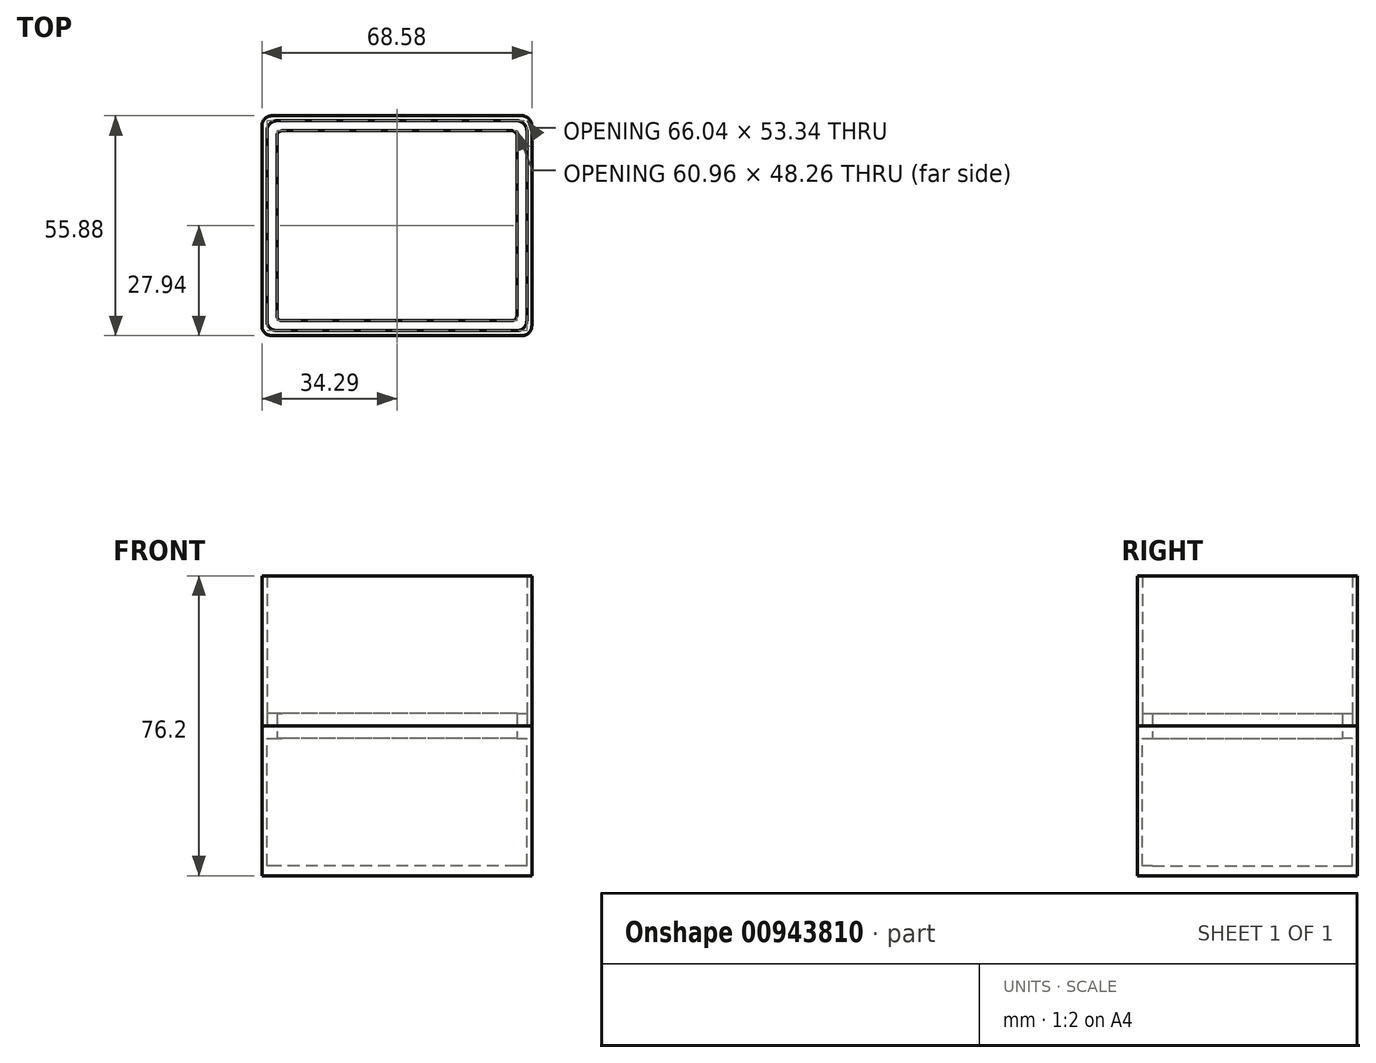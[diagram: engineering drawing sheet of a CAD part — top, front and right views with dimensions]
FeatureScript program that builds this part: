
annotation { "Feature Type Name" : "Feature", "Feature Type Description" : "" }
export const myFeature = defineFeature(function(context is Context, id is Id, definition is map)
    precondition{}
    {
        {
            var Q0;
            Q0=qCreatedBy(makeId("Top.planeOp"),FACE);
            var sketch = newSketch(context, id + "F0", { "sketchPlane" : qUnion([Q0])});
            skLineSegment(sketch, "E0.bottom", {"start": v(31.75, -27.94) * mm, "end": v(-31.75, -27.94) * mm});
            skLineSegment(sketch, "E0.top", {"start": v(31.75, 27.94) * mm, "end": v(-31.75, 27.94) * mm});
            skLineSegment(sketch, "E0.left", {"start": v(34.3, -25.4) * mm, "end": v(34.3, 25.4) * mm});
            skLineSegment(sketch, "E0.right", {"start": v(-34.3, -25.4) * mm, "end": v(-34.3, 25.4) * mm});
            skPoint(sketch, "E0.middle", {"position": v(0, 0) * mm});
            skPoint(sketch, "E1.visualSharp", {"position": v(-34.3, -27.94) * mm});
            skArc(sketch, "E1.filletArc", {"start": v(-34.3, -25.4) * mm, "mid": v(-33.55, -27.2) * mm, "end": v(-31.75, -27.94) * mm});
            skPoint(sketch, "E2.visualSharp", {"position": v(-34.3, 27.94) * mm});
            skArc(sketch, "E2.filletArc", {"start": v(-31.75, 27.94) * mm, "mid": v(-33.55, 27.2) * mm, "end": v(-34.3, 25.4) * mm});
            skPoint(sketch, "E3.visualSharp", {"position": v(34.3, 27.94) * mm});
            skArc(sketch, "E3.filletArc", {"start": v(34.3, 25.4) * mm, "mid": v(33.55, 27.2) * mm, "end": v(31.75, 27.94) * mm});
            skPoint(sketch, "E4.visualSharp", {"position": v(34.3, -27.94) * mm});
            skArc(sketch, "E4.filletArc", {"start": v(31.75, -27.94) * mm, "mid": v(33.55, -27.2) * mm, "end": v(34.3, -25.4) * mm});
            skSolve(sketch);
        }
        {
            var Q0;
            Q0=makeQuery(id+"F0.imprint","IMPRINT",FACE,{"disambiguationData":[TD([[makeQuery(id+"F0.imprint","IMPRINT",EDGE,{"derivedFrom":sQuery(id+"F0.wireOp",EDGE,"E0.bottom")}),-1.0]])]});
            extrude(context, id + "F1", {"entities" : qUnion([Q0]), "depth" : 38.1 * mm, "offsetDistance" : 25.4 * mm});
        }
        {
            var Q0;
            Q0=makeQuery(id+"F1.opExtrude","CAP_FACE",FACE,{"disambiguationData":[OSD([sQuery(id+"F0.wireOp",EDGE,"E0.bottom"),sQuery(id+"F0.wireOp",EDGE,"E0.top"),sQuery(id+"F0.wireOp",EDGE,"E0.left"),sQuery(id+"F0.wireOp",EDGE,"E0.right"),sQuery(id+"F0.wireOp",EDGE,"E1.filletArc"),sQuery(id+"F0.wireOp",EDGE,"E2.filletArc"),sQuery(id+"F0.wireOp",EDGE,"E3.filletArc"),sQuery(id+"F0.wireOp",EDGE,"E4.filletArc")])],"isStart":false});
            var sketch = newSketch(context, id + "F2", { "sketchPlane" : qUnion([Q0])});
            skLineSegment(sketch, "E5.0", {"start": v(30.48, 26.67) * mm, "end": v(-30.48, 26.67) * mm});
            skLineSegment(sketch, "E5.1", {"start": v(33.02, -24.13) * mm, "end": v(33.02, 24.13) * mm});
            skLineSegment(sketch, "E5.2", {"start": v(30.48, -26.67) * mm, "end": v(-30.48, -26.67) * mm});
            skLineSegment(sketch, "E5.3", {"start": v(-33.02, -24.13) * mm, "end": v(-33.02, 24.13) * mm});
            skPoint(sketch, "E6.visualSharp", {"position": v(-33.02, 26.67) * mm});
            skArc(sketch, "E6.filletArc", {"start": v(-30.48, 26.67) * mm, "mid": v(-32.28, 25.93) * mm, "end": v(-33.02, 24.13) * mm});
            skPoint(sketch, "E7.visualSharp", {"position": v(33.02, 26.67) * mm});
            skArc(sketch, "E7.filletArc", {"start": v(33.02, 24.13) * mm, "mid": v(32.28, 25.93) * mm, "end": v(30.48, 26.67) * mm});
            skPoint(sketch, "E8.visualSharp", {"position": v(33.02, -26.67) * mm});
            skArc(sketch, "E8.filletArc", {"start": v(30.48, -26.67) * mm, "mid": v(32.28, -25.93) * mm, "end": v(33.02, -24.13) * mm});
            skPoint(sketch, "E9.visualSharp", {"position": v(-33.02, -26.67) * mm});
            skArc(sketch, "E9.filletArc", {"start": v(-33.02, -24.13) * mm, "mid": v(-32.28, -25.93) * mm, "end": v(-30.48, -26.67) * mm});
            skSolve(sketch);
        }
        {
            var Q0;
            Q0=makeQuery(id+"F2.imprint","IMPRINT",FACE,{"disambiguationData":[TD([[makeQuery(id+"F2.imprint","IMPRINT",EDGE,{"derivedFrom":sQuery(id+"F2.wireOp",EDGE,"E5.0")}),1.0]])]});
            extrude(context, id + "F3", {"entities" : qUnion([Q0]), "operationType" : NewBodyOperationType.REMOVE, "oppositeDirection" : true, "depth" : 35.56 * mm, "offsetDistance" : 25.4 * mm});
        }
        {
            var Q0;
            Q0=makeQuery(id+"F1.opExtrude","CAP_FACE",FACE,{"disambiguationData":[OSD([sQuery(id+"F0.wireOp",EDGE,"E0.bottom"),sQuery(id+"F0.wireOp",EDGE,"E0.top"),sQuery(id+"F0.wireOp",EDGE,"E0.left"),sQuery(id+"F0.wireOp",EDGE,"E0.right"),sQuery(id+"F0.wireOp",EDGE,"E1.filletArc"),sQuery(id+"F0.wireOp",EDGE,"E2.filletArc"),sQuery(id+"F0.wireOp",EDGE,"E3.filletArc"),sQuery(id+"F0.wireOp",EDGE,"E4.filletArc")])],"isStart":false});
            var sketch = newSketch(context, id + "F4", { "sketchPlane" : qUnion([Q0])});
            skLineSegment(sketch, "E10.0", {"start": v(29.21, 24.13) * mm, "end": v(-29.21, 24.13) * mm});
            skLineSegment(sketch, "E10.1", {"start": v(30.48, -22.86) * mm, "end": v(30.48, 22.86) * mm});
            skLineSegment(sketch, "E10.2", {"start": v(29.21, -24.13) * mm, "end": v(-29.21, -24.13) * mm});
            skLineSegment(sketch, "E10.3", {"start": v(-30.48, -22.86) * mm, "end": v(-30.48, 22.86) * mm});
            skPoint(sketch, "E11.visualSharp", {"position": v(-30.48, 24.13) * mm});
            skArc(sketch, "E11.filletArc", {"start": v(-29.21, 24.13) * mm, "mid": v(-30.1, 23.76) * mm, "end": v(-30.48, 22.86) * mm});
            skPoint(sketch, "E12.visualSharp", {"position": v(30.48, 24.13) * mm});
            skArc(sketch, "E12.filletArc", {"start": v(30.48, 22.86) * mm, "mid": v(30.1, 23.76) * mm, "end": v(29.21, 24.13) * mm});
            skPoint(sketch, "E13.visualSharp", {"position": v(30.48, -24.13) * mm});
            skArc(sketch, "E13.filletArc", {"start": v(29.21, -24.13) * mm, "mid": v(30.1, -23.76) * mm, "end": v(30.48, -22.86) * mm});
            skPoint(sketch, "E14.visualSharp", {"position": v(-30.48, -24.13) * mm});
            skArc(sketch, "E14.filletArc", {"start": v(-30.48, -22.86) * mm, "mid": v(-30.1, -23.76) * mm, "end": v(-29.21, -24.13) * mm});
            skSolve(sketch);
        }
        {
            var Q0;
            Q0=makeQuery(id+"F4.imprint","IMPRINT",FACE,{"disambiguationData":[TD([[makeQuery(id+"F4.imprint","IMPRINT",EDGE,{"derivedFrom":sQuery(id+"F4.wireOp",EDGE,"E10.0")}),-1.0]])]});
            extrude(context, id + "F5", {"entities" : qUnion([Q0]), "operationType" : NewBodyOperationType.ADD, "endBound" : BoundingType.SYMMETRIC, "depth" : 6.35 * mm, "offsetDistance" : 25.4 * mm});
        }
        {
            var Q0;
            Q0=makeQuery(id+"F1.opExtrude","CAP_FACE",FACE,{"disambiguationData":[OSD([sQuery(id+"F0.wireOp",EDGE,"E0.bottom"),sQuery(id+"F0.wireOp",EDGE,"E0.top"),sQuery(id+"F0.wireOp",EDGE,"E0.left"),sQuery(id+"F0.wireOp",EDGE,"E0.right"),sQuery(id+"F0.wireOp",EDGE,"E1.filletArc"),sQuery(id+"F0.wireOp",EDGE,"E2.filletArc"),sQuery(id+"F0.wireOp",EDGE,"E3.filletArc"),sQuery(id+"F0.wireOp",EDGE,"E4.filletArc")])],"isStart":false});
            extrude(context, id + "F6", {"entities" : qUnion([Q0]), "depth" : 38.1 * mm, "offsetDistance" : 25.4 * mm});
        }
    });
